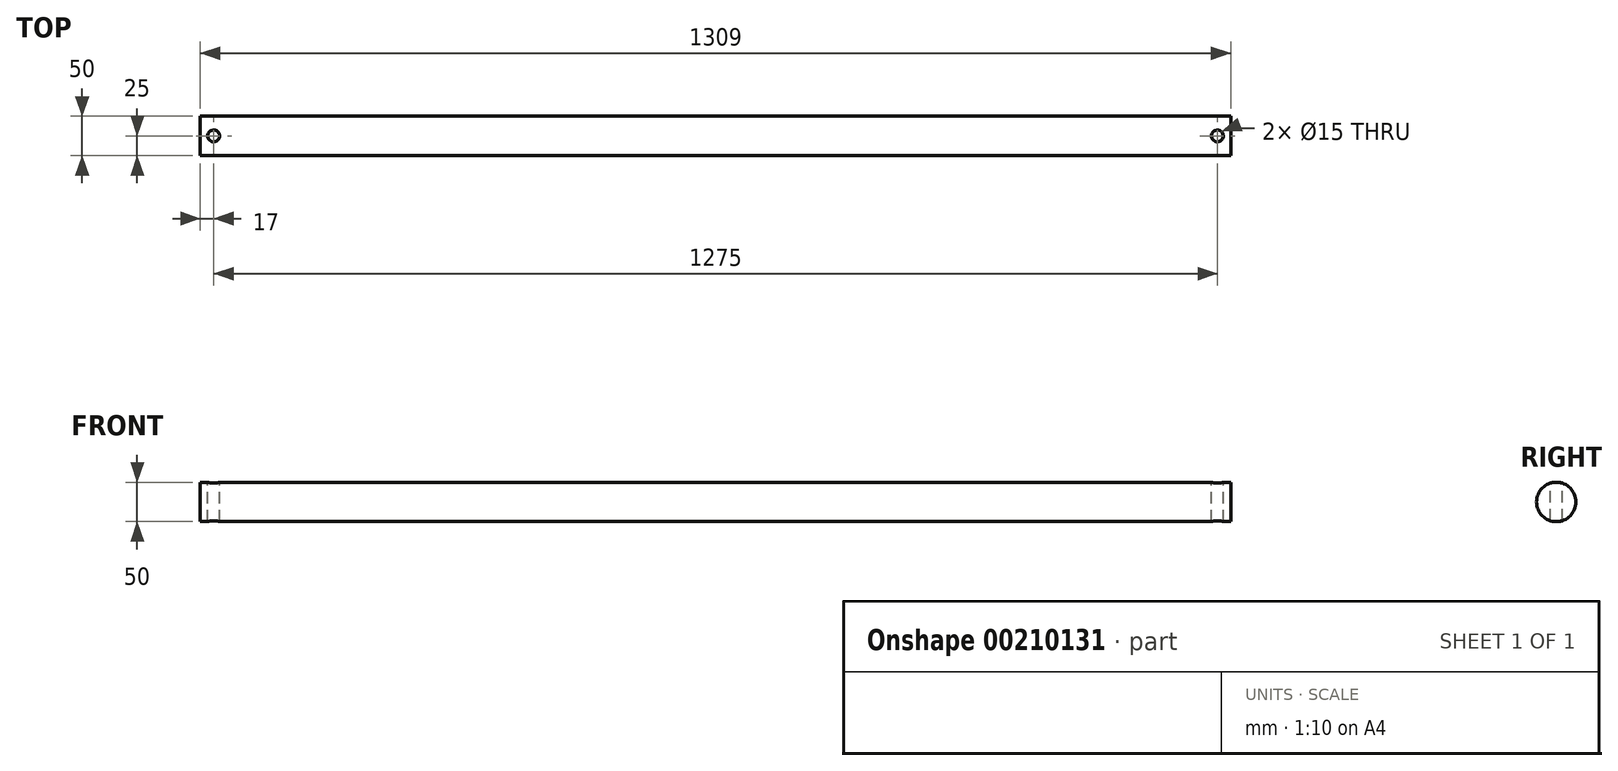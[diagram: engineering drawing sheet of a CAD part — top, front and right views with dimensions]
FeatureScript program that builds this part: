
annotation { "Feature Type Name" : "Feature", "Feature Type Description" : "" }
export const myFeature = defineFeature(function(context is Context, id is Id, definition is map)
    precondition{}
    {
        {
            var Q0;
            Q0=qCreatedBy(makeId("Right.planeOp"),FACE);
            var sketch = newSketch(context, id + "F0", { "sketchPlane" : qUnion([Q0])});
            skCircle(sketch, "E0", {"center": v(0, 0) * mm, "radius": 25 * mm});
            skSolve(sketch);
        }
        {
            var Q0;
            Q0 = qSketchRegion(id + "F0", true);
            extrude(context, id + "F1", {"entities" : qUnion([Q0]), "depth" : 1309 * mm});
        }
        {
            var Q0;
            Q0=qCreatedBy(makeId("Top.planeOp"),FACE);
            var sketch = newSketch(context, id + "F2", { "sketchPlane" : qUnion([Q0])});
            skLineSegment(sketch, "E1", {"start": v(0, 0) * mm, "end": v(17, 0) * mm, "construction": true});
            skLineSegment(sketch, "E2", {"start": v(17, 0) * mm, "end": v(1292, 0) * mm, "construction": true});
            skLineSegment(sketch, "E3", {"start": v(1292, 0) * mm, "end": v(1309, 0) * mm, "construction": true});
            skCircle(sketch, "E4", {"center": v(17, 0) * mm, "radius": 7.5 * mm});
            skCircle(sketch, "E5", {"center": v(1292, 0) * mm, "radius": 7.5 * mm});
            skSolve(sketch);
        }
        {
            var Q0;
            Q0 = qSketchRegion(id + "F2", true);
            extrude(context, id + "F3", {"entities" : qUnion([Q0]), "operationType" : NewBodyOperationType.REMOVE, "endBound" : BoundingType.SYMMETRIC, "oppositeDirection" : true, "depth" : 100 * mm});
        }
    });
